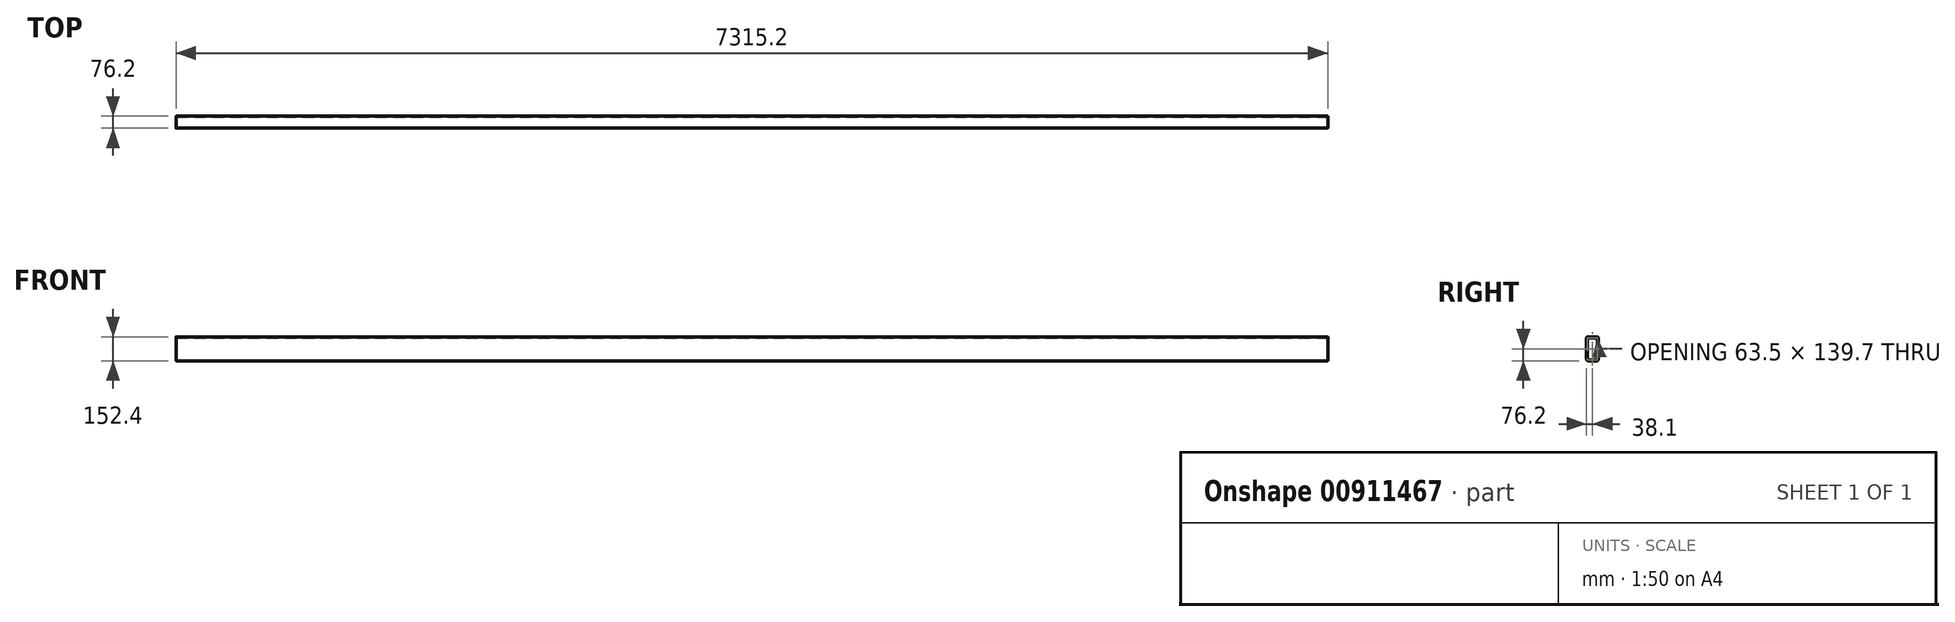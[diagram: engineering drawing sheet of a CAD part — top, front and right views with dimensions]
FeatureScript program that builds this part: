
annotation { "Feature Type Name" : "Feature", "Feature Type Description" : "" }
export const myFeature = defineFeature(function(context is Context, id is Id, definition is map)
    precondition{}
    {
        {
            var Q0;
            Q0=qCreatedBy(makeId("Right.planeOp"),FACE);
            var sketch = newSketch(context, id + "F0", { "sketchPlane" : qUnion([Q0])});
            skLineSegment(sketch, "E0.bottom", {"start": v(28.57, 76.2) * mm, "end": v(-28.58, 76.2) * mm});
            skLineSegment(sketch, "E0.top", {"start": v(28.58, -76.2) * mm, "end": v(-28.57, -76.2) * mm});
            skLineSegment(sketch, "E0.left", {"start": v(38.1, 66.68) * mm, "end": v(38.1, -66.67) * mm});
            skLineSegment(sketch, "E0.right", {"start": v(-38.1, 66.68) * mm, "end": v(-38.1, -66.67) * mm});
            skPoint(sketch, "E0.middle", {"position": v(0, 0) * mm});
            skPoint(sketch, "E1.visualSharp", {"position": v(-38.1, 76.2) * mm});
            skArc(sketch, "E1.filletArc", {"start": v(-28.58, 76.2) * mm, "mid": v(-35.31, 73.41) * mm, "end": v(-38.1, 66.68) * mm});
            skPoint(sketch, "E2.visualSharp", {"position": v(38.1, 76.2) * mm});
            skArc(sketch, "E2.filletArc", {"start": v(38.1, 66.68) * mm, "mid": v(35.31, 73.41) * mm, "end": v(28.57, 76.2) * mm});
            skPoint(sketch, "E3.visualSharp", {"position": v(38.1, -76.2) * mm});
            skArc(sketch, "E3.filletArc", {"start": v(28.58, -76.2) * mm, "mid": v(35.31, -73.41) * mm, "end": v(38.1, -66.67) * mm});
            skPoint(sketch, "E4.visualSharp", {"position": v(-38.1, -76.2) * mm});
            skArc(sketch, "E4.filletArc", {"start": v(-38.1, -66.67) * mm, "mid": v(-35.31, -73.41) * mm, "end": v(-28.57, -76.2) * mm});
            skArc(sketch, "E5.0", {"start": v(-28.58, 69.85) * mm, "mid": v(-30.82, 68.92) * mm, "end": v(-31.75, 66.68) * mm});
            skLineSegment(sketch, "E5.1", {"start": v(28.57, 69.85) * mm, "end": v(-28.58, 69.85) * mm});
            skLineSegment(sketch, "E5.2", {"start": v(-31.75, 66.68) * mm, "end": v(-31.75, -66.67) * mm});
            skArc(sketch, "E5.3", {"start": v(31.75, 66.68) * mm, "mid": v(30.82, 68.92) * mm, "end": v(28.57, 69.85) * mm});
            skArc(sketch, "E5.4", {"start": v(-31.75, -66.67) * mm, "mid": v(-30.82, -68.92) * mm, "end": v(-28.57, -69.85) * mm});
            skLineSegment(sketch, "E5.5", {"start": v(28.58, -69.85) * mm, "end": v(-28.57, -69.85) * mm});
            skArc(sketch, "E5.6", {"start": v(28.58, -69.85) * mm, "mid": v(30.82, -68.92) * mm, "end": v(31.75, -66.67) * mm});
            skLineSegment(sketch, "E5.7", {"start": v(31.75, 66.68) * mm, "end": v(31.75, -66.67) * mm});
            skSolve(sketch);
        }
        {
            var Q0;
            Q0=makeQuery(id+"F0.imprint","IMPRINT",FACE,{"disambiguationData":[TD([[makeQuery(id+"F0.imprint","IMPRINT",EDGE,{"derivedFrom":sQuery(id+"F0.wireOp",EDGE,"E0.bottom")}),1.0]])]});
            extrude(context, id + "F1", {"entities" : qUnion([Q0]), "oppositeDirection" : true, "depth" : 7315.2 * mm, "offsetDistance" : 25.4 * mm});
        }
    });
